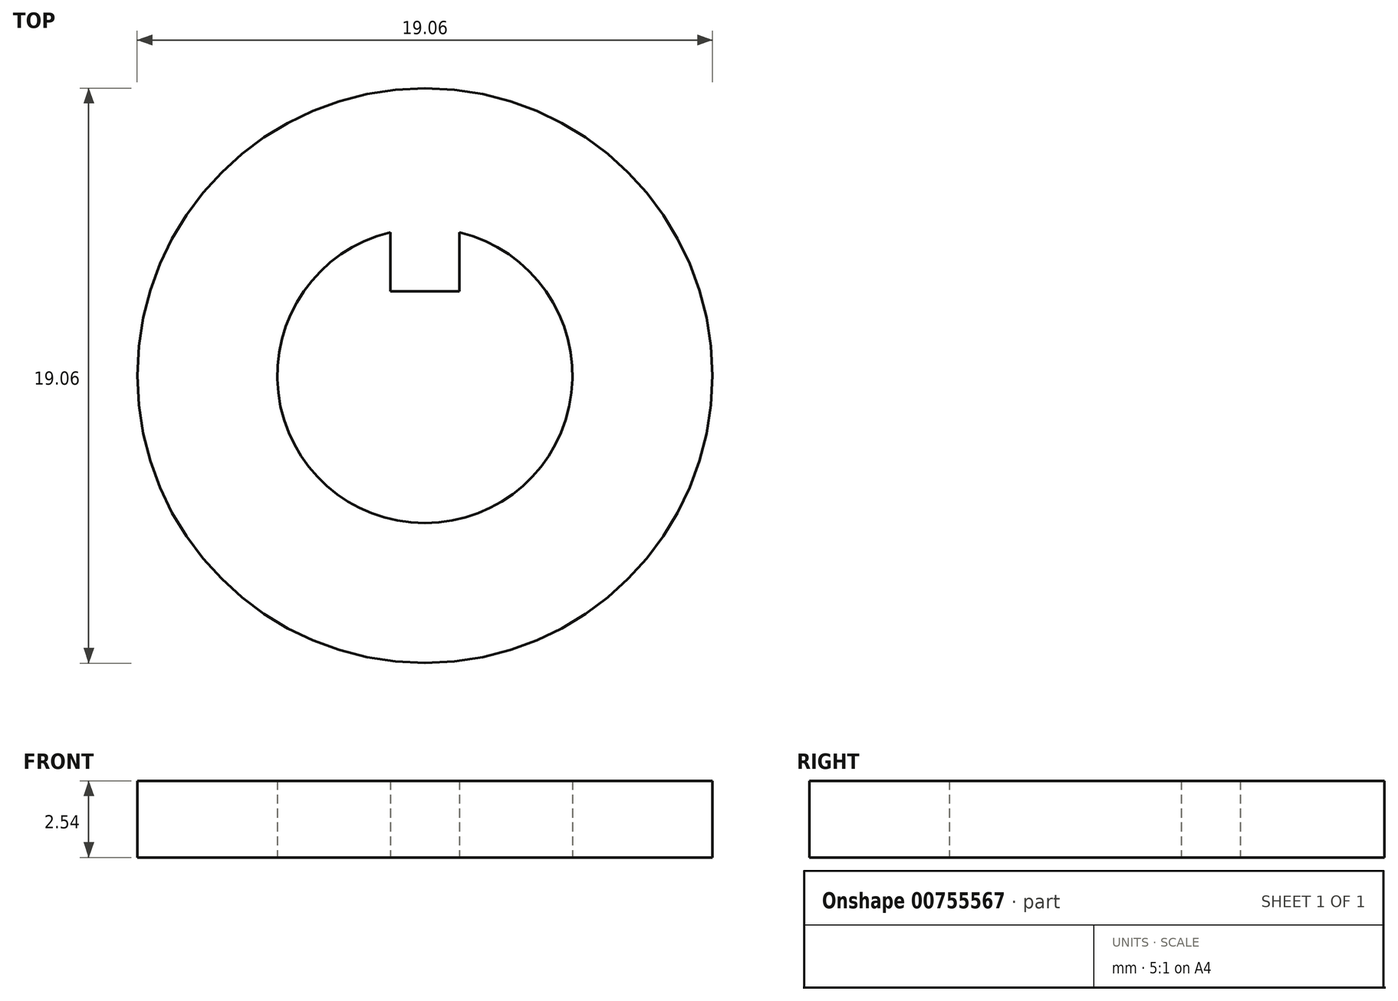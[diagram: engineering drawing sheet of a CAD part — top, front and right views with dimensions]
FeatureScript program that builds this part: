
annotation { "Feature Type Name" : "Feature", "Feature Type Description" : "" }
export const myFeature = defineFeature(function(context is Context, id is Id, definition is map)
    precondition{}
    {
        {
            var Q0;
            Q0=qCreatedBy(makeId("Top.planeOp"),FACE);
            var sketch = newSketch(context, id + "F0", { "sketchPlane" : qUnion([Q0])});
            skArc(sketch, "E0", {"start": v(-1.14, 4.75) * mm, "mid": v(0, -4.89) * mm, "end": v(1.14, 4.75) * mm});
            skLineSegment(sketch, "E1.top", {"start": v(-1.14, 2.8) * mm, "end": v(1.14, 2.8) * mm});
            skLineSegment(sketch, "E1.left", {"start": v(-1.14, 4.75) * mm, "end": v(-1.14, 2.8) * mm});
            skLineSegment(sketch, "E1.right", {"start": v(1.14, 4.75) * mm, "end": v(1.14, 2.8) * mm});
            skCircle(sketch, "E2", {"center": v(0, 0) * mm, "radius": 9.53 * mm});
            skSolve(sketch);
        }
        {
            var Q0;
            Q0 = qSketchRegion(id + "F0", true);
            extrude(context, id + "F1", {"entities" : qUnion([Q0]), "depth" : 2.54 * mm, "offsetDistance" : 25.4 * mm});
        }
    });
